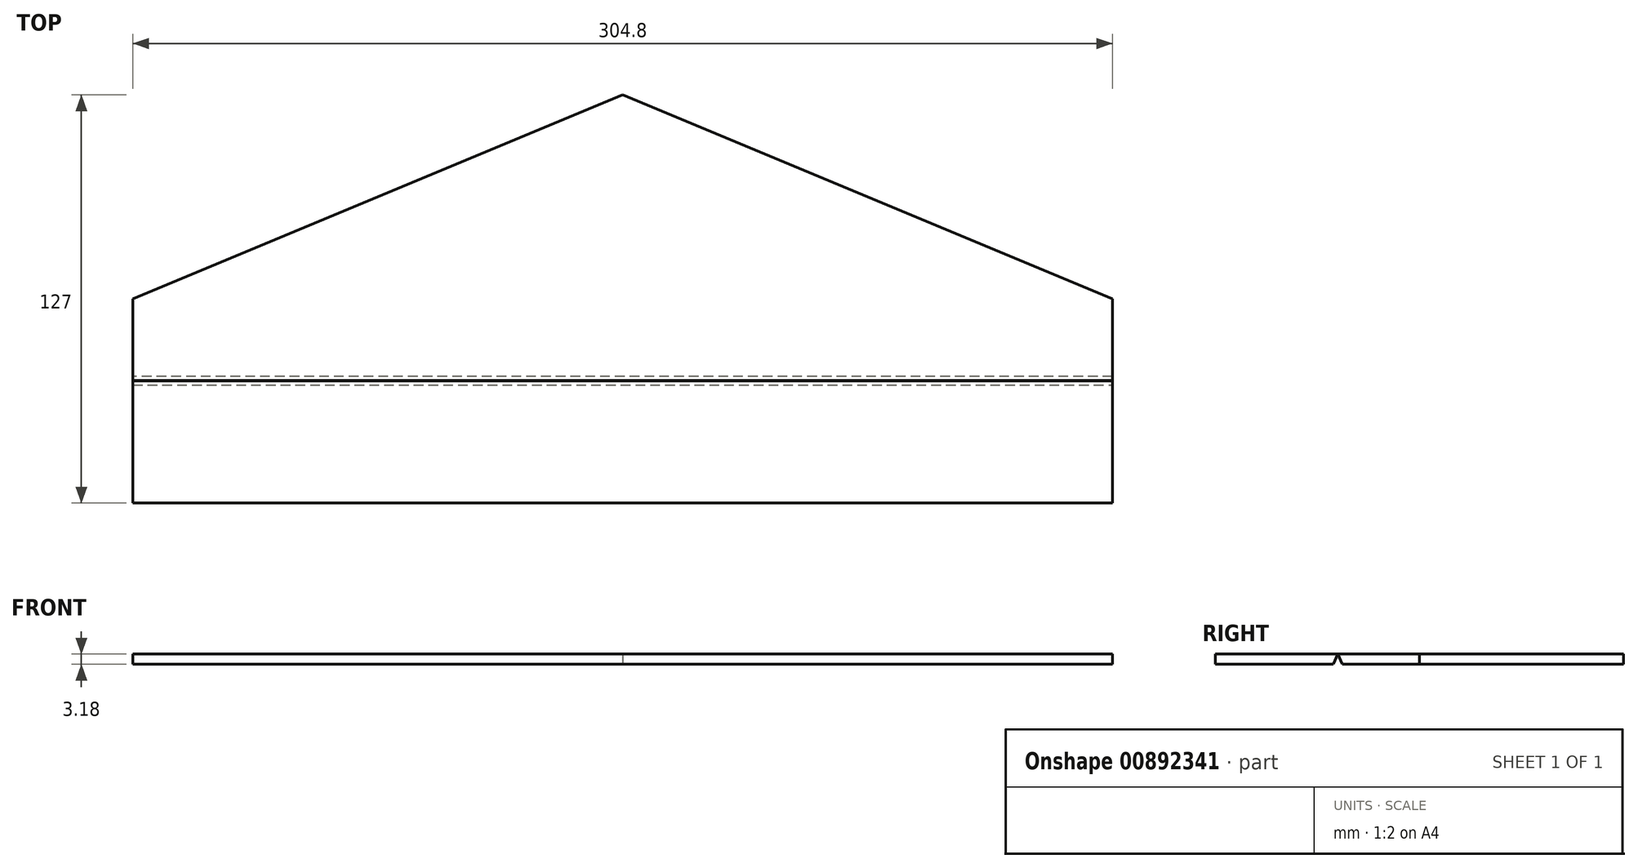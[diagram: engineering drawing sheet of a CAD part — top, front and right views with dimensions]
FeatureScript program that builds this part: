
annotation { "Feature Type Name" : "Feature", "Feature Type Description" : "" }
export const myFeature = defineFeature(function(context is Context, id is Id, definition is map)
    precondition{}
    {
        {
            var Q0;
            Q0=qCreatedBy(makeId("Top.planeOp"),FACE);
            var sketch = newSketch(context, id + "F0", { "sketchPlane" : qUnion([Q0])});
            skLineSegment(sketch, "E0", {"start": v(-152.4, 0) * mm, "end": v(152.4, 0) * mm});
            skLineSegment(sketch, "E1", {"start": v(-152.4, 0) * mm, "end": v(-152.4, 25.4) * mm});
            skLineSegment(sketch, "E2", {"start": v(152.4, 0) * mm, "end": v(152.4, 25.4) * mm});
            skLineSegment(sketch, "E3", {"start": v(152.4, 25.4) * mm, "end": v(0, 88.9) * mm});
            skLineSegment(sketch, "E4", {"start": v(0, 88.9) * mm, "end": v(-152.4, 25.4) * mm});
            skLineSegment(sketch, "E5", {"start": v(-152.4, 0) * mm, "end": v(-152.4, -38.1) * mm});
            skLineSegment(sketch, "E6", {"start": v(-152.4, -38.1) * mm, "end": v(152.4, -38.1) * mm});
            skLineSegment(sketch, "E7", {"start": v(152.4, -38.1) * mm, "end": v(152.4, 0) * mm});
            skLineSegment(sketch, "E8", {"start": v(0, 88.9) * mm, "end": v(0, -38.1) * mm});
            skSolve(sketch);
        }
        {
            var Q0;
            {var subQ0=sQuery(id+"F0.wireOp",EDGE,"E1");Q0=makeQuery(id+"F0.imprint","IMPRINT",FACE,{"disambiguationData":[TD([[makeQuery(id+"F0.imprint","IMPRINT",EDGE,{"derivedFrom":subQ0}),-1.0]])]});}
            var Q1;
            {var subQ0=sQuery(id+"F0.wireOp",EDGE,"E2");Q1=makeQuery(id+"F0.imprint","IMPRINT",FACE,{"disambiguationData":[TD([[makeQuery(id+"F0.imprint","IMPRINT",EDGE,{"derivedFrom":subQ0}),1.0]])]});}
            extrude(context, id + "F1", {"entities" : qUnion([Q0, Q1]), "depth" : 3.17 * mm, "offsetDistance" : 25.4 * mm});
        }
        {
            var Q0;
            {var subQ0=sQuery(id+"F0.wireOp",EDGE,"E5");Q0=makeQuery(id+"F0.imprint","IMPRINT",FACE,{"disambiguationData":[TD([[makeQuery(id+"F0.imprint","IMPRINT",EDGE,{"derivedFrom":subQ0}),1.0]])]});}
            var Q1;
            {var subQ0=sQuery(id+"F0.wireOp",EDGE,"E7");Q1=makeQuery(id+"F0.imprint","IMPRINT",FACE,{"disambiguationData":[TD([[makeQuery(id+"F0.imprint","IMPRINT",EDGE,{"derivedFrom":subQ0}),1.0]])]});}
            extrude(context, id + "F2", {"entities" : qUnion([Q0, Q1]), "depth" : 3.17 * mm, "offsetDistance" : 25.4 * mm});
        }
        {
            var Q0;
            Q0=makeQuery(id+"F1.opExtrude","CAP_EDGE",EDGE,{"disambiguationData":[OSD([sQuery(id+"F0.wireOp",EDGE,"E0")])],"isStart":true});
            chamfer(context, id + "F3", {"entities" : qUnion([Q0]), "chamferType" : ChamferType.OFFSET_ANGLE, "width" : 3.3 * mm, "oppositeDirection" : false, "angle" : 22.5 * degree});
        }
        {
            var Q0;
            Q0=makeQuery(id+"F2.opExtrude","CAP_EDGE",EDGE,{"disambiguationData":[OSD([sQuery(id+"F0.wireOp",EDGE,"E0")])],"isStart":true});
            chamfer(context, id + "F4", {"entities" : qUnion([Q0]), "chamferType" : ChamferType.OFFSET_ANGLE, "width" : 3.3 * mm, "oppositeDirection" : true, "angle" : 22.5 * degree, "tangentPropagation" : true});
        }
    });
